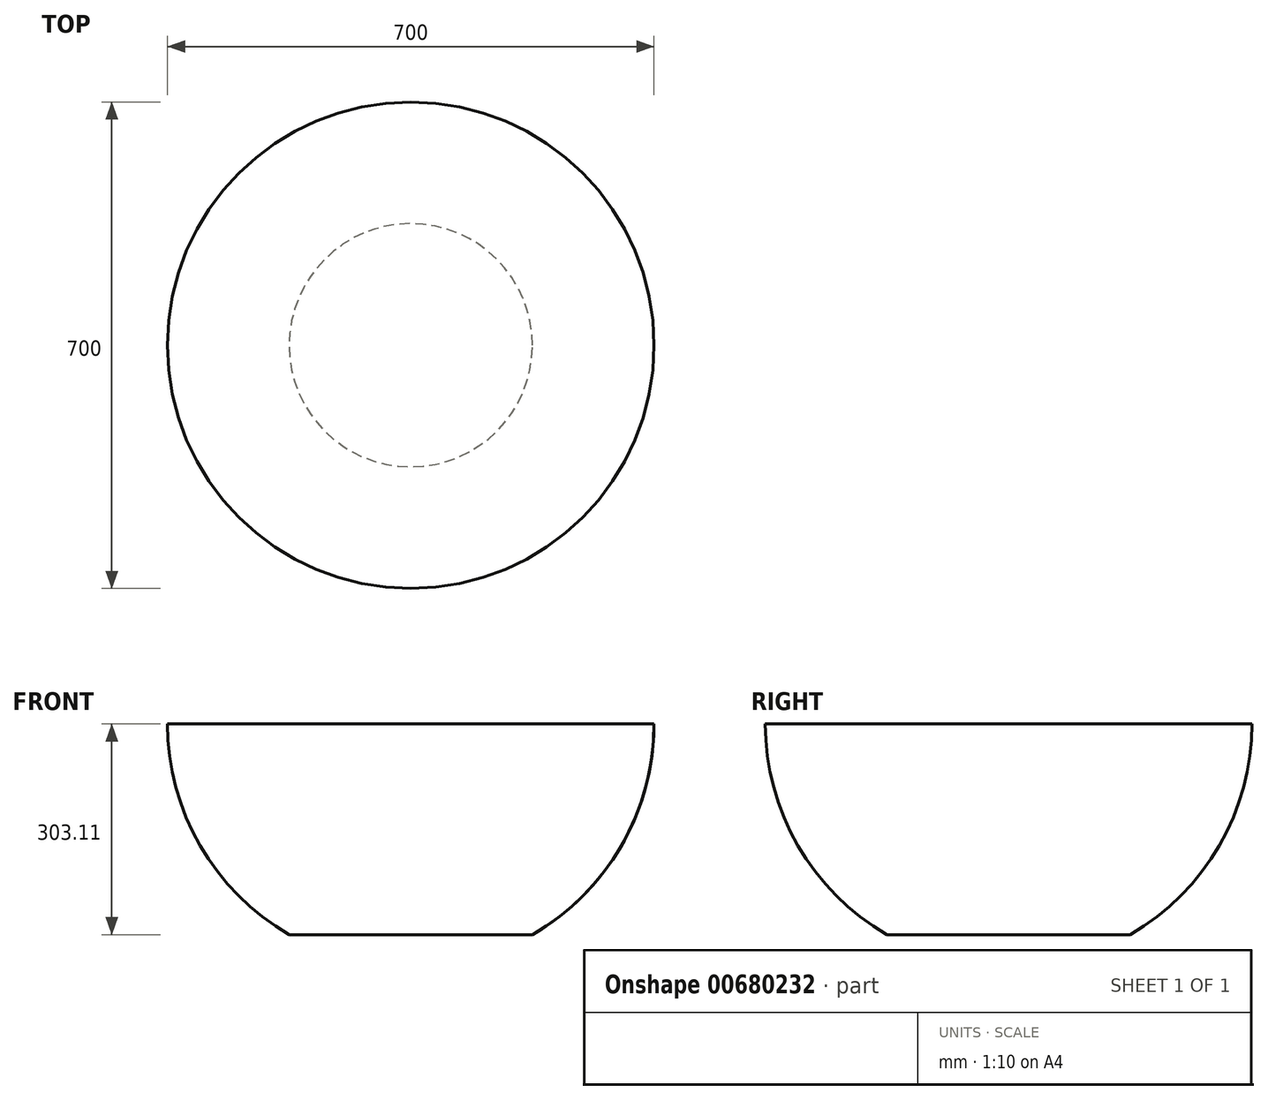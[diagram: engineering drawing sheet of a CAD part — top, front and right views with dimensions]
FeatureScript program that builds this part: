
annotation { "Feature Type Name" : "Feature", "Feature Type Description" : "" }
export const myFeature = defineFeature(function(context is Context, id is Id, definition is map)
    precondition{}
    {
        {
            var Q0;
            Q0=qCreatedBy(makeId("Front.planeOp"),FACE);
            var sketch = newSketch(context, id + "F0", { "sketchPlane" : qUnion([Q0])});
            skArc(sketch, "E0", {"start": v(-350, 0) * mm, "mid": v(-303.1, -175) * mm, "end": v(-175, -303.1) * mm});
            skLineSegment(sketch, "E1", {"start": v(-350, 0) * mm, "end": v(0, 0) * mm});
            skLineSegment(sketch, "E2", {"start": v(-175, -303.1) * mm, "end": v(0, -303.1) * mm});
            skLineSegment(sketch, "E3", {"start": v(0, 0) * mm, "end": v(0, -303.1) * mm});
            skPoint(sketch, "E4.orphan", {"position": v(175, -303.1) * mm});
            skSolve(sketch);
        }
        {
            var Q0;
            Q0=makeQuery(id+"F0.imprint","IMPRINT",FACE,{"disambiguationData":[TD([[makeQuery(id+"F0.imprint","IMPRINT",EDGE,{"derivedFrom":sQuery(id+"F0.wireOp",EDGE,"E0")}),1.0]])]});
            var Q1;
            Q1=sQuery(id+"F0.wireOp",EDGE,"E3");
            revolve(context, id + "F1", {"entities" : qUnion([Q0]), "axis" : qUnion([Q1]), "revolveType" : RevolveType.FULL});
        }
    });
